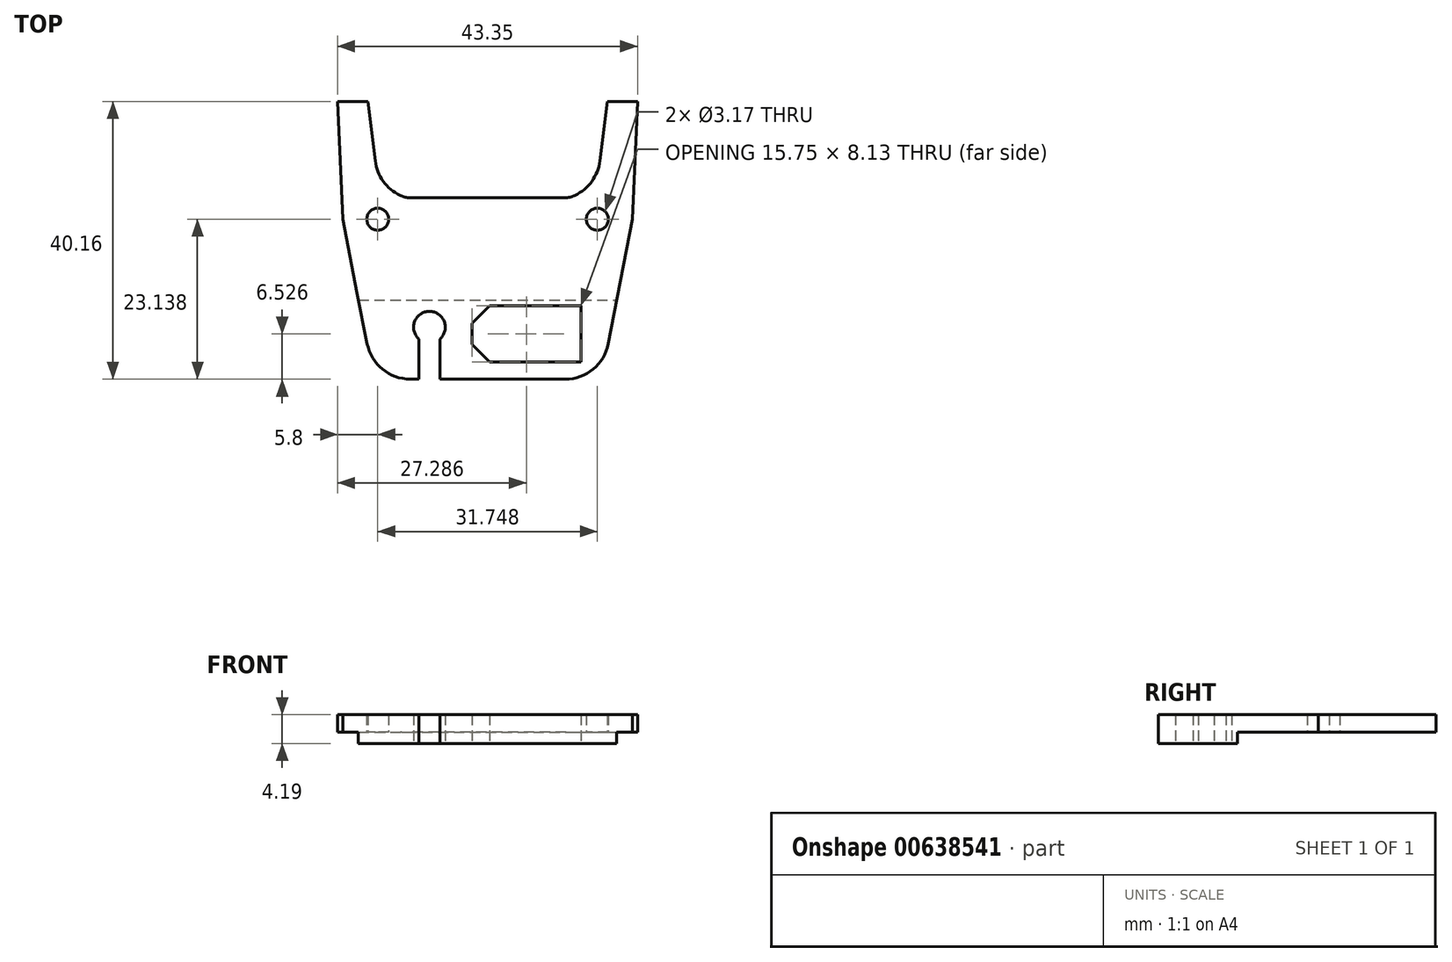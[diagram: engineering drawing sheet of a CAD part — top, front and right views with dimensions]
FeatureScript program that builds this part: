
annotation { "Feature Type Name" : "Feature", "Feature Type Description" : "" }
export const myFeature = defineFeature(function(context is Context, id is Id, definition is map)
    precondition{}
    {
        {
            var Q0;
            Q0=qCreatedBy(makeId("Top.planeOp"),FACE);
            var sketch = newSketch(context, id + "F0", { "sketchPlane" : qUnion([Q0])});
            skLineSegment(sketch, "E0", {"start": v(-1.27, -1.12) * mm, "end": v(-1.27, 7.01) * mm});
            skLineSegment(sketch, "E1", {"start": v(-1.27, 7.01) * mm, "end": v(-14.48, 7.01) * mm});
            skLineSegment(sketch, "E2", {"start": v(-14.48, 7.01) * mm, "end": v(-17.02, 4.47) * mm});
            skLineSegment(sketch, "E3", {"start": v(-17.02, 4.47) * mm, "end": v(-17.02, 1.42) * mm});
            skLineSegment(sketch, "E4", {"start": v(-17.02, 1.42) * mm, "end": v(-14.48, -1.12) * mm});
            skLineSegment(sketch, "E5", {"start": v(-14.48, -1.12) * mm, "end": v(-1.27, -1.12) * mm});
            skLineSegment(sketch, "E6", {"start": v(-3.42, 22.67) * mm, "end": v(-26.1, 22.67) * mm});
            skCircle(sketch, "E7", {"center": v(-30.63, 19.56) * mm, "radius": 1.59 * mm});
            skCircle(sketch, "E8", {"center": v(1.12, 19.56) * mm, "radius": 1.59 * mm});
            skLineSegment(sketch, "E9", {"start": v(6.16, 19.56) * mm, "end": v(4.11, 8.9) * mm});
            skLineSegment(sketch, "E10", {"start": v(-35.67, 19.56) * mm, "end": v(-33.62, 8.89) * mm});
            skLineSegment(sketch, "E11", {"start": v(6.16, 19.56) * mm, "end": v(6.92, 36.58) * mm});
            skLineSegment(sketch, "E12", {"start": v(-35.67, 19.56) * mm, "end": v(-36.43, 36.58) * mm});
            skLineSegment(sketch, "E13", {"start": v(-2.35, 22.9) * mm, "end": v(-2.13, 23) * mm});
            skLineSegment(sketch, "E14", {"start": v(-27.17, 22.9) * mm, "end": v(-27.38, 23) * mm});
            skLineSegment(sketch, "E15", {"start": v(-31, 27.99) * mm, "end": v(-32.05, 36.58) * mm});
            skLineSegment(sketch, "E16", {"start": v(1.48, 27.99) * mm, "end": v(2.54, 36.58) * mm});
            skLineSegment(sketch, "E17", {"start": v(2.54, 36.58) * mm, "end": v(6.92, 36.58) * mm});
            skLineSegment(sketch, "E18", {"start": v(-36.43, 36.58) * mm, "end": v(-32.05, 36.58) * mm});
            skPoint(sketch, "E19.visualSharp", {"position": v(-2.86, 22.67) * mm});
            skArc(sketch, "E19.filletArc", {"start": v(-3.42, 22.67) * mm, "mid": v(-2.87, 22.73) * mm, "end": v(-2.35, 22.9) * mm});
            skPoint(sketch, "E20.visualSharp", {"position": v(-26.66, 22.67) * mm});
            skArc(sketch, "E20.filletArc", {"start": v(-27.17, 22.9) * mm, "mid": v(-26.64, 22.73) * mm, "end": v(-26.1, 22.67) * mm});
            skPoint(sketch, "E21.visualSharp", {"position": v(-30.57, 24.5) * mm});
            skArc(sketch, "E21.filletArc", {"start": v(-31, 27.99) * mm, "mid": v(-29.83, 25.03) * mm, "end": v(-27.38, 23) * mm});
            skPoint(sketch, "E22.visualSharp", {"position": v(1.05, 24.5) * mm});
            skArc(sketch, "E22.filletArc", {"start": v(-2.13, 23) * mm, "mid": v(0.32, 25.03) * mm, "end": v(1.48, 27.99) * mm});
            skLineSegment(sketch, "E23", {"start": v(-33.62, 8.89) * mm, "end": v(-32.15, 1.54) * mm});
            skLineSegment(sketch, "E24", {"start": v(4.11, 8.9) * mm, "end": v(2.7, 1.57) * mm});
            skLineSegment(sketch, "E25", {"start": v(-3.53, -3.58) * mm, "end": v(-21.63, -3.57) * mm});
            skPoint(sketch, "E26.visualSharp", {"position": v(-31.13, -3.56) * mm});
            skArc(sketch, "E26.filletArc", {"start": v(-32.15, 1.54) * mm, "mid": v(-29.95, -2.13) * mm, "end": v(-25.93, -3.57) * mm});
            skPoint(sketch, "E27.visualSharp", {"position": v(1.71, -3.58) * mm});
            skArc(sketch, "E27.filletArc", {"start": v(-3.53, -3.58) * mm, "mid": v(0.51, -2.13) * mm, "end": v(2.7, 1.57) * mm});
            skLineSegment(sketch, "E28", {"start": v(-24.69, 2.23) * mm, "end": v(-24.69, -3.57) * mm});
            skLineSegment(sketch, "E29", {"start": v(-21.64, 2.23) * mm, "end": v(-21.64, -3.57) * mm});
            skArc(sketch, "E30", {"start": v(-21.64, 2.23) * mm, "mid": v(-23.16, 6.22) * mm, "end": v(-24.69, 2.23) * mm});
            skLineSegment(sketch, "E31", {"start": v(-24.69, -3.57) * mm, "end": v(-24.69, -3.57) * mm});
            skLineSegment(sketch, "E32", {"start": v(-24.69, -3.57) * mm, "end": v(-25.93, -3.57) * mm});
            skLineSegment(sketch, "E33", {"start": v(-21.63, -3.57) * mm, "end": v(-21.64, -3.57) * mm});
            skLineSegment(sketch, "E34", {"start": v(-33.42, 7.87) * mm, "end": v(3.92, 7.87) * mm});
            skSolve(sketch);
        }
        {
            var Q0;
            Q0=makeQuery(id+"F0.imprint","IMPRINT",FACE,{"disambiguationData":[TD([[makeQuery(id+"F0.imprint","IMPRINT",EDGE,{"derivedFrom":sQuery(id+"F0.wireOp",EDGE,"E6")}),1.0]])]});
            extrude(context, id + "F1", {"entities" : qUnion([Q0]), "depth" : 2.54 * mm, "offsetDistance" : 25.4 * mm});
        }
        {
            var Q0;
            Q0=makeQuery(id+"F0.imprint","IMPRINT",FACE,{"disambiguationData":[TD([[makeQuery(id+"F0.imprint","IMPRINT",EDGE,{"derivedFrom":sQuery(id+"F0.wireOp",EDGE,"E0")}),-1.0]])]});
            extrude(context, id + "F2", {"entities" : qUnion([Q0]), "operationType" : NewBodyOperationType.ADD, "depth" : 2.54 * mm, "offsetDistance" : 25.4 * mm});
        }
        {
            var Q0;
            Q0=makeQuery(id+"F0.imprint","IMPRINT",FACE,{"disambiguationData":[TD([[makeQuery(id+"F0.imprint","IMPRINT",EDGE,{"derivedFrom":sQuery(id+"F0.wireOp",EDGE,"E0")}),-1.0]])]});
            extrude(context, id + "F3", {"entities" : qUnion([Q0]), "operationType" : NewBodyOperationType.ADD, "oppositeDirection" : true, "depth" : 1.65 * mm, "offsetDistance" : 25.4 * mm});
        }
    });
